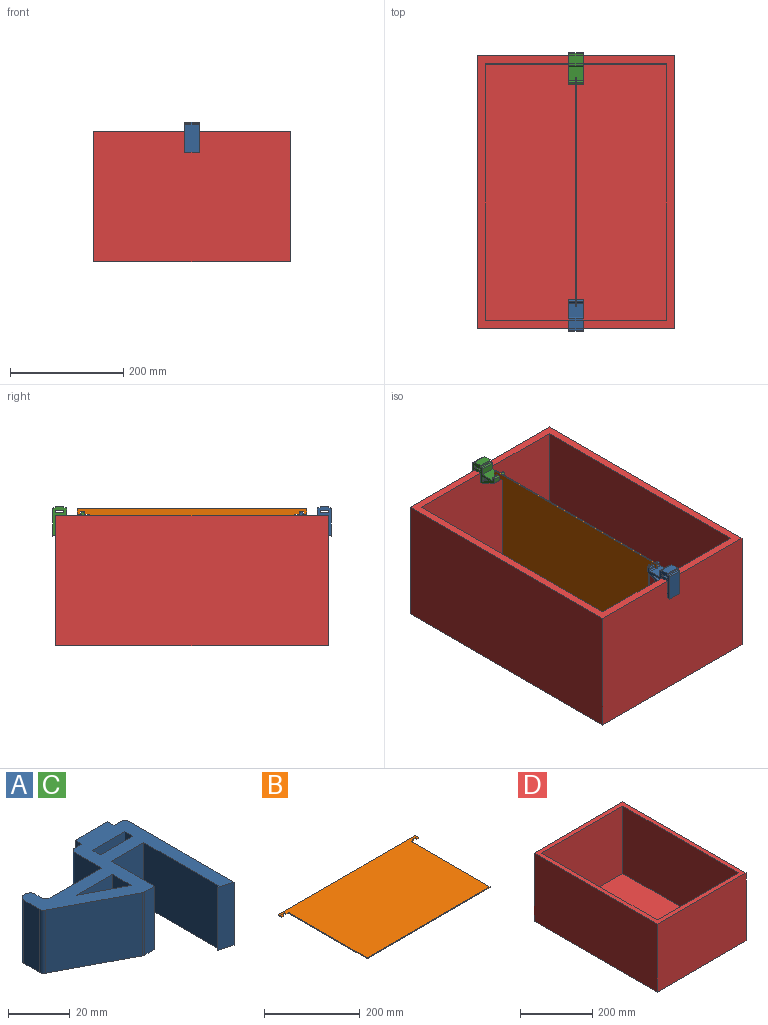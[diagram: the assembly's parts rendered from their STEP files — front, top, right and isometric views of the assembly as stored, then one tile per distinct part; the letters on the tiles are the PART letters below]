
ASSEMBLY  parts=4 mates=3
PART A: 34 faces, bbox 55.3x52.9x25 mm
  f0: plane 25x3mm, normal (0,1,0), area 75mm2, adj f1,f25,f26,f33
  f1: plane 25x3.04mm, normal (1,0,0), area 76mm2, adj f0,f2,f25,f26
  f2: plane 25x14.8mm, normal (0,1,0), area 370mm2, adj f1,f3,f25,f26
  f3: plane 25x3.04mm, normal (-1,0,0), area 76mm2, adj f2,f4,f25,f26
  f4: plane 25x3mm, normal (0,1,0), area 75mm2, adj f3,f25,f26,f27
  f5: plane 25x12mm, normal (-1,0,0), area 300mm2, adj f6,f25,f26,f27
  f6: plane 25x23.5mm, normal (0,1,0), area 587.5mm2, adj f5,f25,f26,f28
  f7: plane 25x3mm, normal (1,0,0), area 75mm2, adj f25,f26,f28,f29
  f8: plane 25x1mm, normal (0,1,0), area 25mm2, adj f25,f26,f29,f30
  f9: plane 25x7.15mm, normal (-1,0,0), area 178.9mm2, adj f25,f26,f30,f31
  f10: plane 28.99x25mm, normal (-0.46,-0.89,0), area 818.1mm2, adj f25,f26,f31,f32
  f11: plane 25x4.51mm, normal (0,-1,0), area 112.7mm2, adj f12,f25,f26,f32
  f12: plane 25x19.71mm, normal (1,0,0), area 492.6mm2, adj f11,f13,f25,f26
  f13: plane 25x14.8mm, normal (0,-1,0), area 370mm2, adj f12,f14,f25,f26
  f14: plane 34.2x25mm, normal (-1,0,0), area 855mm2, adj f13,f15,f25,f26
  f15: plane 25x0.86mm, normal (-0.5,0.86,0), area 25mm2, adj f14,f16,f25,f26
  f16: plane 25x5.86mm, normal (-0.25,-0.97,0), area 151.6mm2, adj f15,f24,f25,f26
  f17: plane 25x14.8mm, normal (0,-1,0), area 370mm2, adj f18,f22,f25,f26
  f18: plane 25x3.63mm, normal (-1,0,0), area 90.7mm2, adj f17,f19,f25,f26
  f19: plane 25x14.8mm, normal (0,1,0), area 370mm2, adj f18,f22,f25,f26
  f20: plane 25x16.6mm, normal (0.46,0.89,0), area 468.4mm2, adj f21,f23,f25,f26
  f21: plane 25x16.6mm, normal (0,-1,0), area 414.9mm2, adj f20,f23,f25,f26
  f22: plane 25x3.63mm, normal (1,0,0), area 90.7mm2, adj f17,f19,f25,f26
  f23: plane 25x8.69mm, normal (-1,0,0), area 217.3mm2, adj f20,f21,f25,f26
  f24: plane 47.88x25mm, normal (1,0,0), area 1196.9mm2, adj f16,f25,f26,f33
  f25: plane 55.3x52.92mm, normal (0,0,1), area 912.3mm2, adj f0,f1,f2,f3,f4,f5,f6,f7
  f26: plane 55.3x52.92mm, normal (0,0,-1), area 912.3mm2, adj f0,f1,f2,f3,f4,f5,f6,f7
  f27: cylinder r=2mm len=25mm, axis (0,0,-1), area 78.5mm2, adj f4,f5,f25,f26
  f28: cylinder r=2mm len=25mm, axis (0,0,1), area 78.5mm2, adj f6,f7,f25,f26
  f29: cylinder r=2mm len=25mm, axis (0,0,-1), area 78.5mm2, adj f7,f8,f25,f26
  f30: cylinder r=2mm len=25mm, axis (0,0,-1), area 78.5mm2, adj f8,f9,f25,f26
  f31: cylinder r=2mm len=25mm, axis (0,0,-1), area 54.4mm2, adj f9,f10,f25,f26
  f32: cylinder r=2mm len=25mm, axis (0,0,-1), area 24.1mm2, adj f10,f11,f25,f26
  f33: cylinder r=2mm len=25mm, axis (0,0,-1), area 78.5mm2, adj f0,f24,f25,f26
PART B: 18 faces, bbox 405x242x2.2 mm
  f0: plane 232x2.2mm, normal (1,0,0), area 510.4mm2, adj f1,f15,f16,f17
  f1: plane 7.4x2.2mm, normal (0,-1,0), area 16.3mm2, adj f0,f2,f16,f17
  f2: plane 4.6x2.2mm, normal (1,0,0), area 10.1mm2, adj f1,f3,f16,f17
  f3: plane 8x2.2mm, normal (0,-1,0), area 17.6mm2, adj f2,f4,f16,f17
  f4: plane 4.6x2.2mm, normal (-1,0,0), area 10.1mm2, adj f3,f5,f16,f17
  f5: plane 5.6x2.2mm, normal (0,-1,0), area 12.3mm2, adj f4,f6,f16,f17
  f6: plane 10x2.2mm, normal (1,0,0), area 22mm2, adj f5,f7,f16,f17
  f7: plane 405x2.2mm, normal (0,1,0), area 891mm2, adj f6,f8,f16,f17
  f8: plane 10x2.2mm, normal (-1,0,0), area 22mm2, adj f7,f9,f16,f17
  f9: plane 5.6x2.2mm, normal (0,-1,0), area 12.3mm2, adj f8,f10,f16,f17
  f10: plane 4.6x2.2mm, normal (1,0,0), area 10.1mm2, adj f9,f11,f16,f17
  f11: plane 8x2.2mm, normal (0,-1,0), area 17.6mm2, adj f10,f12,f16,f17
  f12: plane 4.6x2.2mm, normal (-1,0,0), area 10.1mm2, adj f11,f13,f16,f17
  f13: plane 7.4x2.2mm, normal (0,-1,0), area 16.3mm2, adj f12,f14,f16,f17
  f14: plane 232x2.2mm, normal (-1,0,0), area 510.4mm2, adj f13,f15,f16,f17
  f15: plane 363x2.2mm, normal (0,-1,0), area 798.6mm2, adj f0,f14,f16,f17
  f16: plane 405x242mm, normal (0,0,1), area 88192.4mm2, adj f0,f1,f2,f3,f4,f5,f6,f7
  f17: plane 405x242mm, normal (0,0,-1), area 88192.4mm2, adj f0,f1,f2,f3,f4,f5,f6,f7
PART C: same geometry as A
PART D: 11 faces, bbox 347x481x230 mm
  f0: plane 481x230mm, normal (1,0,0), area 110630mm2, adj f1,f7,f8,f9
  f1: plane 347x230mm, normal (0,1,0), area 79810mm2, adj f0,f2,f8,f9
  f2: plane 481x230mm, normal (-1,0,0), area 110630mm2, adj f1,f7,f8,f9
  f3: plane 452x228mm, normal (1,0,0), area 103056mm2, adj f4,f6,f8,f10
  f4: plane 318x228mm, normal (0,-1,0), area 72504mm2, adj f3,f5,f8,f10
  f5: plane 452x228mm, normal (-1,0,0), area 103056mm2, adj f4,f6,f8,f10
  f6: plane 318x228mm, normal (0,1,0), area 72504mm2, adj f3,f5,f8,f10
  f7: plane 347x230mm, normal (0,-1,0), area 79810mm2, adj f0,f2,f8,f9
  f8: plane 481x347mm, normal (0,0,1), area 23171mm2, adj f0,f1,f2,f3,f4,f5,f6,f7
  f9: plane 481x347mm, normal (0,0,-1), area 166907mm2, adj f0,f1,f2,f7
  f10: plane 452x318mm, normal (0,0,1), area 143736mm2, adj f3,f4,f5,f6
PLACE A rot(axis=(0.58,-0.58,-0.58),120deg) t=(-171.61,-319.39,161.67)mm
PLACE B rot(axis=(0.58,0.58,0.58),120deg) t=(-185.21,-71.37,51.85)mm
PLACE C rot(axis=(0.58,0.58,0.58),120deg) t=(-196.61,176.75,161.67)mm
PLACE D t=(-184.11,-71.32,-66.2)mm
MATE fastened B.f3 <-> C.f8  axis (0,0,-1) through (-184.11,121.53,170.43)mm
MATE fastened A.f13 <-> D.f8  axis (0,0,-1) through (-184.11,-304.57,163.8)mm
MATE fastened C.f13 <-> D.f8  axis (0,0,-1) through (-184.11,161.93,163.8)mm
